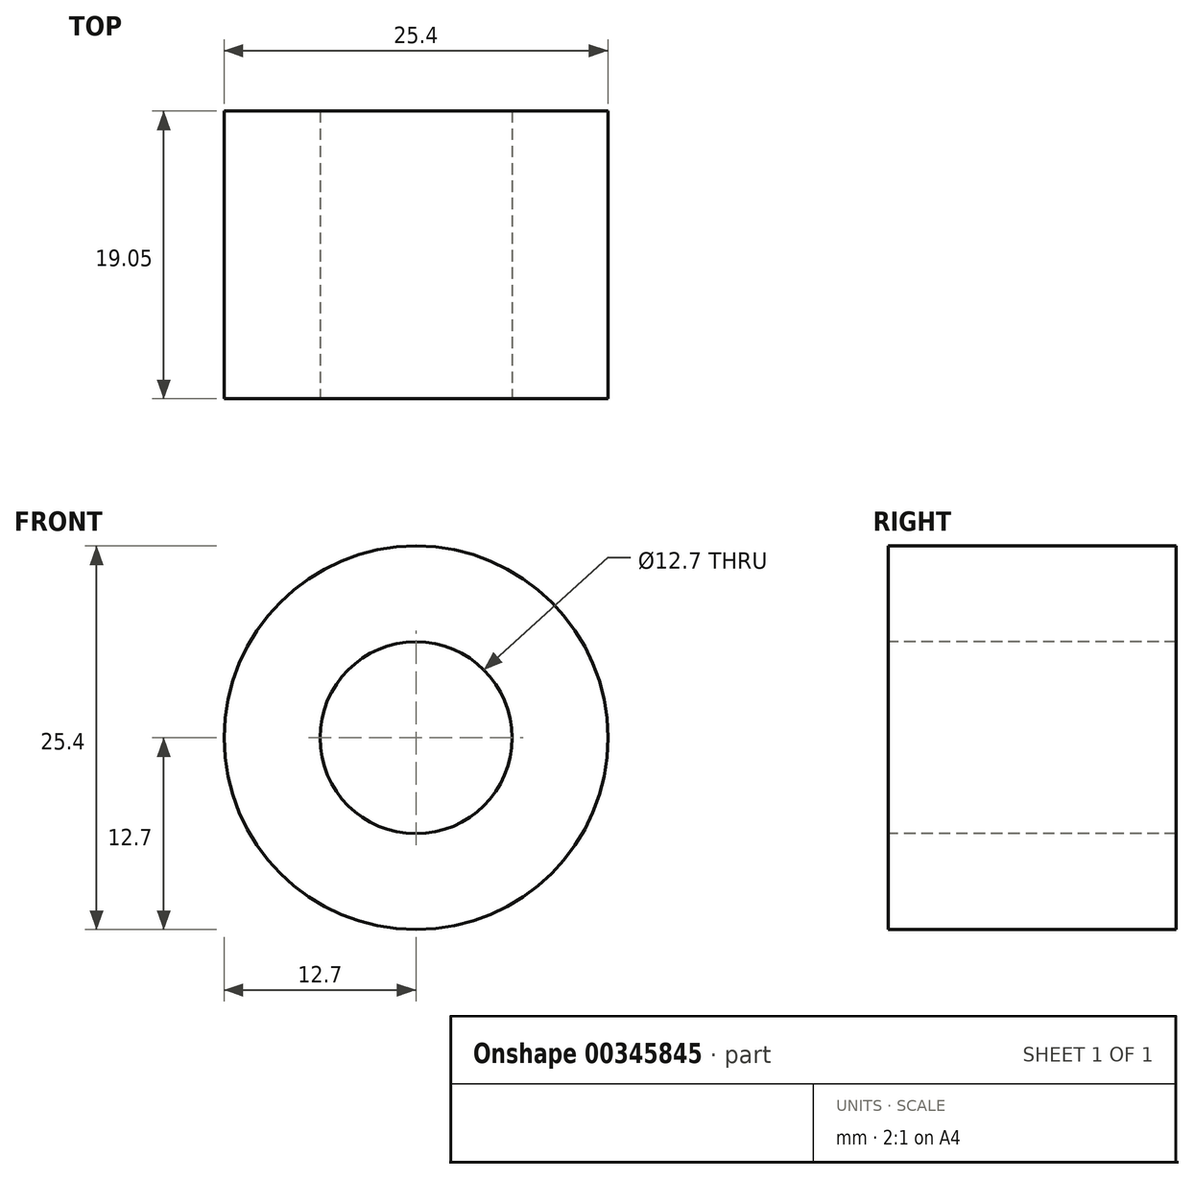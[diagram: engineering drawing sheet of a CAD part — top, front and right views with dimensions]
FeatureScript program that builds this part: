
annotation { "Feature Type Name" : "Feature", "Feature Type Description" : "" }
export const myFeature = defineFeature(function(context is Context, id is Id, definition is map)
    precondition{}
    {
        {
            var Q0;
            Q0=qCreatedBy(makeId("Front.planeOp"),FACE);
            var sketch = newSketch(context, id + "F1", { "sketchPlane" : qUnion([Q0])});
            skCircle(sketch, "E0", {"center": v(0, 0) * mm, "radius": 12.7 * mm});
            skCircle(sketch, "E1", {"center": v(0, 0) * mm, "radius": 6.35 * mm});
            skSolve(sketch);
        }
        {
            var Q0;
            Q0=makeQuery(id+"F1.imprint","IMPRINT",FACE,{"disambiguationData":[TD([[makeQuery(id+"F1.imprint","IMPRINT",EDGE,{"derivedFrom":sQuery(id+"F1.wireOp",EDGE,"E0")}),1.0]])]});
            extrude(context, id + "F0", {"entities" : qUnion([Q0]), "oppositeDirection" : true, "depth" : 19.05 * mm});
        }
    });
